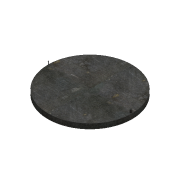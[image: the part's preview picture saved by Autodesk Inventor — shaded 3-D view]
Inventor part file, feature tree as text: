
AUTODESK INVENTOR PART (.ipt)
format: ipt  version: 2017 (Build 210142000, 142)  size: 99,840 bytes
history: native  units: mm
features: extrude x3, sketch x3
ambient origin geometry x8: Origin, YZ Plane, XZ Plane, XY Plane, X Axis, Y Axis, Z Axis, Center Point
bodies: Solid1 (feature_tree)
feature tree (6):
  extrude  "Extrusion1"  Depth=15.0mm TaperAngle=0.0deg
  extrude  "Extrusion2"  Depth=10.0mm TaperAngle=0.0deg
  extrude  "Extrusion3"  [1 undecoded]
  sketch  "Sketch1"  dims[d0=250.0mm d1=15.0mm d2=0.0mm]
  sketch  "Sketch2"  dims[d3=2.0mm d4=10.0mm d5=0.0mm]
  sketch  "Sketch3"  dims[d6=10.0mm d7=0.0mm]
note: 1 required parameter value undecoded (feature->parameter linkage not recoverable at this tier; creation-order binding heuristic only, values carry confidence <= 0.55)
